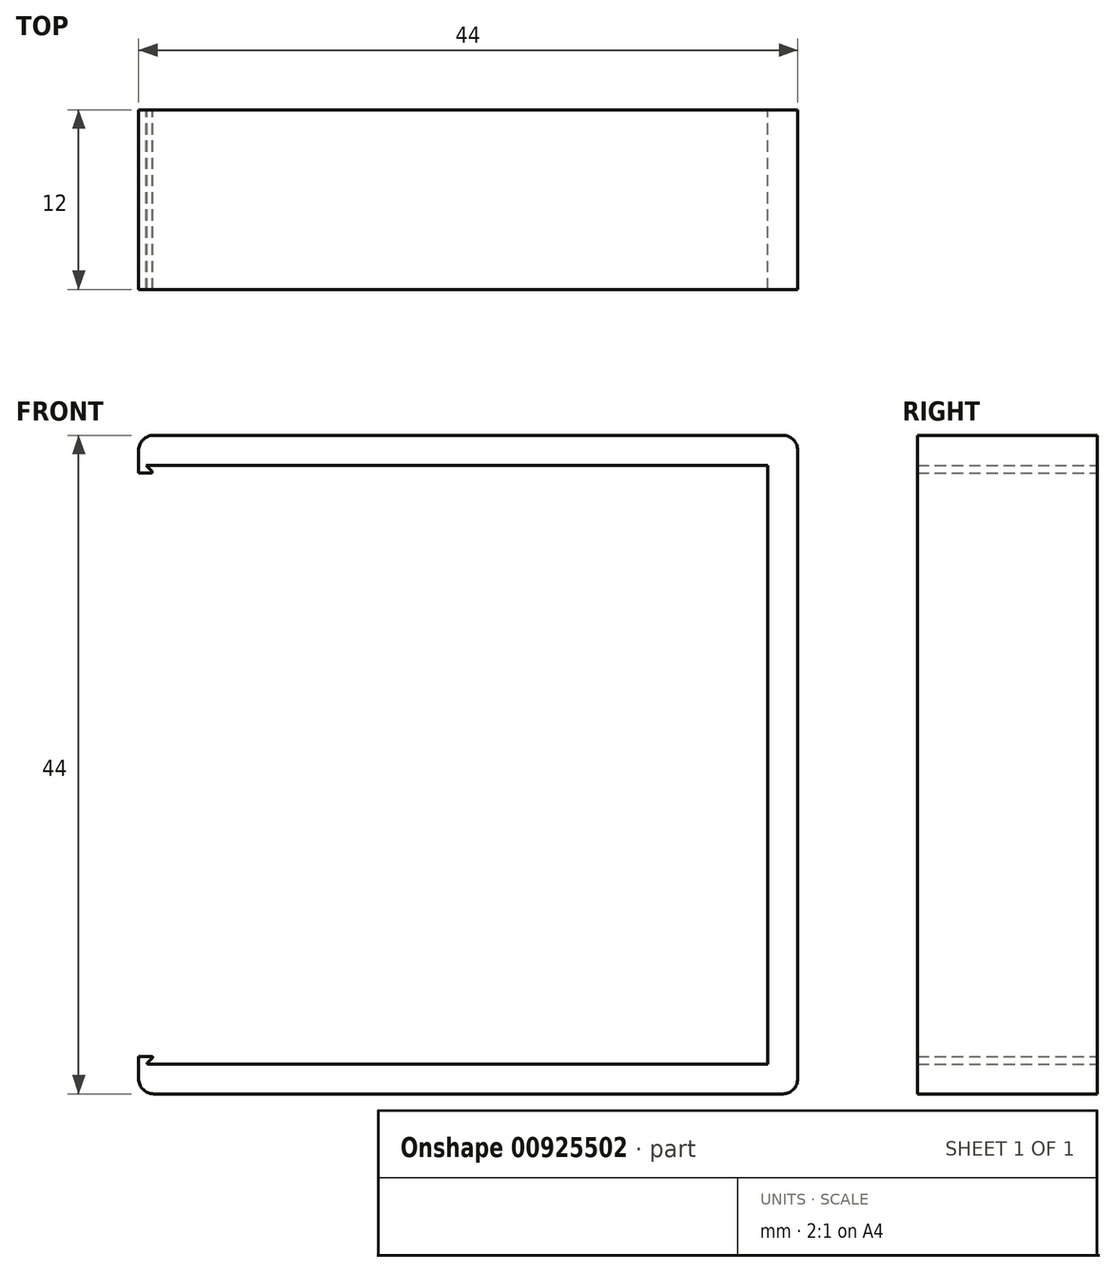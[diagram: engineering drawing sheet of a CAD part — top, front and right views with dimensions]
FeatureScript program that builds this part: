
annotation { "Feature Type Name" : "Feature", "Feature Type Description" : "" }
export const myFeature = defineFeature(function(context is Context, id is Id, definition is map)
    precondition{}
    {
        {
            var Q0;
            Q0=qCreatedBy(makeId("Front.planeOp"),FACE);
            var sketch = newSketch(context, id + "F0", { "sketchPlane" : qUnion([Q0])});
            skLineSegment(sketch, "E0.bottom", {"start": v(20, 20) * mm, "end": v(-20, 20) * mm});
            skLineSegment(sketch, "E0.top", {"start": v(20, -20) * mm, "end": v(-20, -20) * mm});
            skLineSegment(sketch, "E0.left", {"start": v(20, 20) * mm, "end": v(20, -20) * mm});
            skPoint(sketch, "E0.middle", {"position": v(0, 0) * mm});
            skLineSegment(sketch, "E1.0", {"start": v(21, -22) * mm, "end": v(-21, -22) * mm});
            skLineSegment(sketch, "E1.1", {"start": v(22, 21) * mm, "end": v(22, -21) * mm});
            skLineSegment(sketch, "E1.2", {"start": v(21, 22) * mm, "end": v(-21, 22) * mm});
            skLineSegment(sketch, "E1.3", {"start": v(-22, 21) * mm, "end": v(-22, 19.5) * mm});
            skPoint(sketch, "E2.visualSharp", {"position": v(22, 22) * mm});
            skArc(sketch, "E2.filletArc", {"start": v(22, 21) * mm, "mid": v(21.7, 21.7) * mm, "end": v(21, 22) * mm});
            skPoint(sketch, "E3.visualSharp", {"position": v(22, -22) * mm});
            skArc(sketch, "E3.filletArc", {"start": v(21, -22) * mm, "mid": v(21.7, -21.7) * mm, "end": v(22, -21) * mm});
            skPoint(sketch, "E4.visualSharp", {"position": v(-22, -22) * mm});
            skArc(sketch, "E4.filletArc", {"start": v(-22, -21) * mm, "mid": v(-21.7, -21.7) * mm, "end": v(-21, -22) * mm});
            skPoint(sketch, "E5.visualSharp", {"position": v(-22, 22) * mm});
            skArc(sketch, "E5.filletArc", {"start": v(-21, 22) * mm, "mid": v(-21.7, 21.7) * mm, "end": v(-22, 21) * mm});
            skLineSegment(sketch, "E6", {"start": v(-20, 20) * mm, "end": v(-21.5, 20) * mm});
            skLineSegment(sketch, "E7", {"start": v(-21.5, 20) * mm, "end": v(-21.1, 19.6) * mm});
            skLineSegment(sketch, "E8", {"start": v(-21.13, 19.5) * mm, "end": v(-22, 19.5) * mm});
            skLineSegment(sketch, "E9", {"start": v(-26.06, 0) * mm, "end": v(36.17, 0) * mm, "construction": true});
            skLineSegment(sketch, "E10.MirrorCS", {"start": v(-20, -20) * mm, "end": v(-21.38, -20) * mm});
            skLineSegment(sketch, "E11.MirrorCS", {"start": v(-21.41, -19.91) * mm, "end": v(-21.09, -19.59) * mm});
            skLineSegment(sketch, "E12.MirrorCS", {"start": v(-21.12, -19.5) * mm, "end": v(-22, -19.5) * mm});
            skPoint(sketch, "E13.orphan", {"position": v(-22, -20) * mm});
            skPoint(sketch, "E14.orphan", {"position": v(-22, 20) * mm});
            skPoint(sketch, "E15.visualSharp", {"position": v(-21, 19.5) * mm});
            skArc(sketch, "E15.filletArc", {"start": v(-21.13, 19.5) * mm, "mid": v(-21.08, 19.53) * mm, "end": v(-21.1, 19.6) * mm});
            skLineSegment(sketch, "E16.trimOffspring", {"start": v(-22, -19.5) * mm, "end": v(-22, -21) * mm});
            skPoint(sketch, "E17.visualSharp", {"position": v(-21.38, 19.95) * mm});
            skPoint(sketch, "E18.visualSharp", {"position": v(-20, 19.95) * mm});
            skPoint(sketch, "E19.visualSharp", {"position": v(-22, 19.45) * mm});
            skPoint(sketch, "E20.visualSharp", {"position": v(-20.88, 19.45) * mm});
            skPoint(sketch, "E21.visualSharp", {"position": v(-21.38, -19.95) * mm});
            skPoint(sketch, "E22.visualSharp", {"position": v(-21.5, -20) * mm});
            skArc(sketch, "E22.filletArc", {"start": v(-21.41, -19.91) * mm, "mid": v(-21.43, -19.97) * mm, "end": v(-21.38, -20) * mm});
            skPoint(sketch, "E23.visualSharp", {"position": v(-20, -19.95) * mm});
            skPoint(sketch, "E24.visualSharp", {"position": v(-21, -19.5) * mm});
            skArc(sketch, "E24.filletArc", {"start": v(-21.09, -19.59) * mm, "mid": v(-21.07, -19.53) * mm, "end": v(-21.12, -19.5) * mm});
            skPoint(sketch, "E25.visualSharp", {"position": v(-20.88, -19.45) * mm});
            skPoint(sketch, "E26.MirrorCS.end.orphan", {"position": v(-22, -19.45) * mm});
            skSolve(sketch);
        }
        {
            var Q0;
            Q0=makeQuery(id+"F0.imprint","IMPRINT",FACE,{"disambiguationData":[TD([[makeQuery(id+"F0.imprint","IMPRINT",EDGE,{"derivedFrom":sQuery(id+"F0.wireOp",EDGE,"E0.bottom")}),-1.0]])]});
            extrude(context, id + "F1", {"entities" : qUnion([Q0]), "depth" : 12 * mm, "offsetDistance" : 25 * mm});
        }
    });
